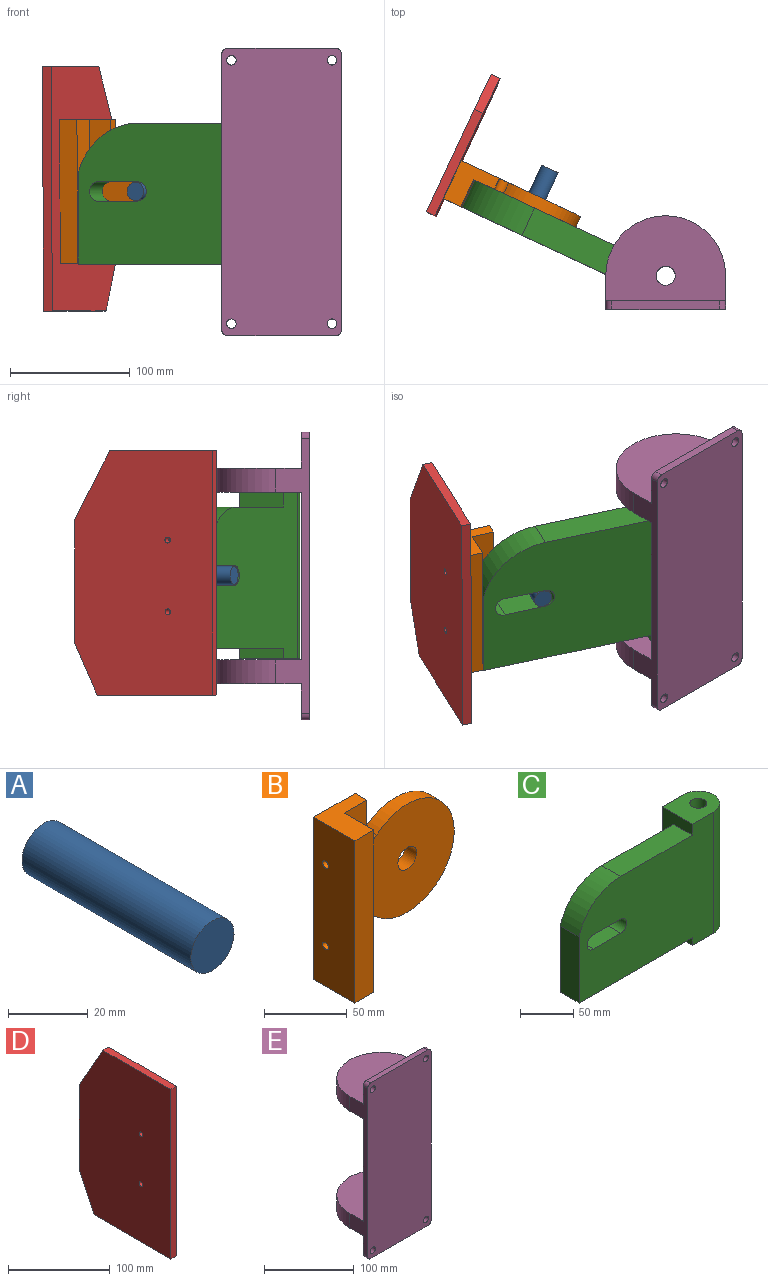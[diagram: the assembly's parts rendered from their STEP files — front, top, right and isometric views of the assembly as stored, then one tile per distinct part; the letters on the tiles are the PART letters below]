
ASSEMBLY  parts=5 mates=4
PART A: 3 faces, bbox 15.4x60x15.4 mm
  f0: cylinder r=7.68mm len=60mm, axis (0,-1,0), area 2896.6mm2, adj f1,f2
  f1: plane 15.37x15.37mm, normal (0,1,0), area 185.5mm2, adj f0
  f2: plane 15.37x15.37mm, normal (0,-1,0), area 185.5mm2, adj f0
PART B: 17 faces, bbox 109.7x35x119.9 mm
  f0: plane 119.85x93.68mm, normal (0,-1,0), area 6944.7mm2, adj f1,f3,f4,f5,f6,f7,f8,f9
  f1: plane 119.85x25mm, normal (1,0,0), area 2977.4mm2, adj f0,f3,f9,f12,f14,f16
  f2: plane 119.85x35mm, normal (-1,0,0), area 4155.5mm2, adj f3,f9,f11,f12,f14,f16
  f3: plane 35.11x35mm, normal (0,0,1), area 751.1mm2, adj f0,f1,f2,f4,f11,f12
  f4: plane 26.27x10mm, normal (1,0,0), area 262.7mm2, adj f0,f3,f5,f11
  f5: cylinder r=5mm len=10mm, axis (0,-1,0), area 114.4mm2, adj f0,f4,f6,f11
  f6: cylinder r=40mm len=80mm, axis (0,-1,0), area 1830.4mm2, adj f0,f5,f7,f11
  f7: cylinder r=5mm len=10mm, axis (0,-1,0), area 114.4mm2, adj f0,f6,f8,f11
  f8: plane 25.75x10mm, normal (1,0,0), area 257.5mm2, adj f0,f7,f9,f11
  f9: plane 35.11x35mm, normal (0,0,-1), area 751.1mm2, adj f0,f1,f2,f8,f11,f12
  f10: cylinder r=8mm len=16mm, axis (0,-1,0), area 502.7mm2, adj f0,f11
  f11: plane 119.85x109.68mm, normal (0,1,0), area 8952.3mm2, adj f2,f3,f4,f5,f6,f7,f8,f9
  f12: plane 119.85x16mm, normal (0,-1,0), area 1917.6mm2, adj f1,f2,f3,f9
  f13: plane 5x2.57mm, normal (-1,0,0), area 10.2mm2, adj f0,f14
  f14: cylinder r=2.5mm len=25mm, axis (-1,0,0), area 323.3mm2, adj f0,f1,f2,f13
  f15: plane 5x2.57mm, normal (-1,0,0), area 10.2mm2, adj f0,f16
  f16: cylinder r=2.5mm len=25mm, axis (-1,0,0), area 323.3mm2, adj f0,f1,f2,f15
PART C: 16 faces, bbox 198.2x40x139.1 mm
  f0: plane 48.17x40mm, normal (0,0,1), area 1553.9mm2, adj f2,f3,f4,f5,f15
  f1: plane 48.17x40mm, normal (0,0,-1), area 1553.9mm2, adj f2,f3,f4,f5,f15
  f2: plane 139.12x40mm, normal (-1,0,0), area 2622.9mm2, adj f0,f1,f3,f4,f6,f13,f14
  f3: plane 139.12x28.17mm, normal (0,1,0), area 3918.7mm2, adj f0,f1,f2,f15
  f4: plane 178.17x139.12mm, normal (0,-1,0), area 20172.5mm2, adj f0,f1,f2,f6,f7,f8,f9,f10
  f5: cylinder r=8mm len=139.12mm, axis (0,0,1), area 6993.1mm2, adj f0,f1
  f6: plane 150x25mm, normal (0,0,-1), area 3750mm2, adj f2,f4,f7,f14
  f7: plane 75.86x25mm, normal (-1,0,0), area 1896.5mm2, adj f4,f6,f8,f14
  f8: cylinder r=57.08mm len=55mm, axis (0,-1,0), area 1855.3mm2, adj f4,f7,f13,f14
  f9: cylinder r=8mm len=25mm, axis (0,-1,0), area 628.3mm2, adj f4,f10,f12,f14
  f10: plane 35.97x25mm, normal (-0.01,0,-1), area 899.4mm2, adj f4,f9,f11,f14
  f11: cylinder r=8.31mm len=25mm, axis (0,-1,0), area 656.2mm2, adj f4,f10,f12,f14
  f12: plane 35.97x25mm, normal (-0.01,0,1), area 899.4mm2, adj f4,f9,f11,f14
  f13: plane 95x25mm, normal (0,0,1), area 2375mm2, adj f2,f4,f8,f14
  f14: plane 150x117.68mm, normal (0,1,0), area 16253.8mm2, adj f2,f6,f7,f8,f9,f10,f11,f12
  f15: cylinder r=20mm len=139.12mm, axis (0,0,1), area 8741.4mm2, adj f0,f1,f3,f4
PART D: 10 faces, bbox 8x127x203.9 mm
  f0: plane 203.88x8mm, normal (0,-1,0), area 1631mm2, adj f1,f7,f8,f9
  f1: plane 94.45x8mm, normal (0,0,1), area 755.6mm2, adj f0,f2,f8,f9
  f2: plane 57.59x32.54mm, normal (0,0.87,0.49), area 529.2mm2, adj f1,f3,f8,f9
  f3: plane 103.27x8mm, normal (0,1,0), area 826.1mm2, adj f2,f4,f8,f9
  f4: plane 43.02x20.47mm, normal (0,0.9,-0.43), area 381.1mm2, adj f3,f7,f8,f9
  f5: cylinder r=2.5mm len=8mm, axis (1,0,0), area 125.7mm2, adj f8,f9
  f6: cylinder r=2.5mm len=8mm, axis (1,0,0), area 125.7mm2, adj f8,f9
  f7: plane 106.52x8mm, normal (0,0,-1), area 852.1mm2, adj f0,f4,f8,f9
  f8: plane 203.88x126.99mm, normal (-1,0,0), area 24473.9mm2, adj f0,f1,f2,f3,f4,f5,f6,f7
  f9: plane 203.88x126.99mm, normal (1,0,0), area 24473.9mm2, adj f0,f1,f2,f3,f4,f5,f6,f7
PART E: 24 faces, bbox 100x78x240 mm
  f0: plane 230x28mm, normal (-1,0,0), area 2450mm2, adj f8,f9,f10,f11,f12,f13,f16,f17
  f1: plane 230x28mm, normal (1,0,0), area 2450mm2, adj f8,f9,f10,f11,f12,f14,f15,f17
  f2: plane 90x7mm, normal (0,0,-1), area 630mm2, adj f8,f11,f13,f14
  f3: plane 90x7mm, normal (0,0,1), area 630mm2, adj f8,f9,f15,f16
  f4: cylinder r=4mm len=8mm, axis (0,1,0), area 175.9mm2, adj f8,f9
  f5: cylinder r=4mm len=8mm, axis (0,1,0), area 175.9mm2, adj f8,f9
  f6: cylinder r=4mm len=8mm, axis (0,1,0), area 175.9mm2, adj f8,f11
  f7: cylinder r=4mm len=8mm, axis (0,1,0), area 175.9mm2, adj f8,f11
  f8: plane 240x100mm, normal (0,-1,0), area 23777.5mm2, adj f0,f1,f2,f3,f4,f5,f6,f7
  f9: plane 100x30mm, normal (0,1,0), area 2888.7mm2, adj f0,f1,f3,f4,f5,f10,f15,f16
  f10: plane 100x71mm, normal (0,0,1), area 5825.9mm2, adj f0,f1,f9,f22,f23
  f11: plane 100x30mm, normal (0,1,0), area 2888.7mm2, adj f0,f1,f2,f6,f7,f12,f13,f14
  f12: plane 100x71mm, normal (0,0,-1), area 5825.9mm2, adj f0,f1,f11,f20,f21
  f13: cylinder r=5mm len=7mm, axis (0,-1,0), area 55mm2, adj f0,f2,f8,f11
  f14: cylinder r=5mm len=7mm, axis (0,1,0), area 55mm2, adj f1,f2,f8,f11
  f15: cylinder r=5mm len=7mm, axis (0,-1,0), area 55mm2, adj f1,f3,f8,f9
  f16: cylinder r=5mm len=7mm, axis (0,1,0), area 55mm2, adj f0,f3,f8,f9
  f17: plane 140x100mm, normal (0,1,0), area 14000mm2, adj f0,f1,f18,f19
  f18: plane 100x71mm, normal (0,0,-1), area 5825.9mm2, adj f0,f1,f17,f22,f23
  f19: plane 100x71mm, normal (0,0,1), area 5825.9mm2, adj f0,f1,f17,f20,f21
  f20: cylinder r=8mm len=20mm, axis (0,0,-1), area 1005.3mm2, adj f12,f19
  f21: cylinder r=50mm len=100mm, axis (0,0,-1), area 3141.6mm2, adj f0,f1,f12,f19
  f22: cylinder r=8mm len=20mm, axis (0,0,-1), area 1005.3mm2, adj f10,f18
  f23: cylinder r=50mm len=100mm, axis (0,0,-1), area 3141.6mm2, adj f0,f1,f10,f18
PLACE A rot(axis=(0.22,0.98,-0.04),161.4deg) t=(-757.89,-1004.08,-52.11)mm
PLACE B rot(axis=(0,-0.01,-1),25deg) t=(-362.15,-719.69,-11.36)mm
PLACE C rot(axis=(0,0,-1),25deg) t=(-190.4,-358.42,-12.01)mm
PLACE D rot(axis=(0,-0.01,-1),25deg) t=(162.14,-509.04,-7.63)mm
PLACE E t=(-47.97,9,-12.45)mm fixed
MATE pin_slot A.f0 <-> C.f4  axis (-0.42,-0.91,0) through (-169.99,-18.17,-12.01)mm
MATE fastened D.f6 <-> B.f14  axis (0.91,-0.42,0.01) through (-222.69,34.07,17.62)mm
MATE revolute C.f5 <-> E.f20  axis (0,0,1) through (-47.97,-53,57.55)mm
MATE revolute A.f0 <-> B.f6  axis (-0.42,-0.91,0) through (-157.31,9.02,-12.01)mm
